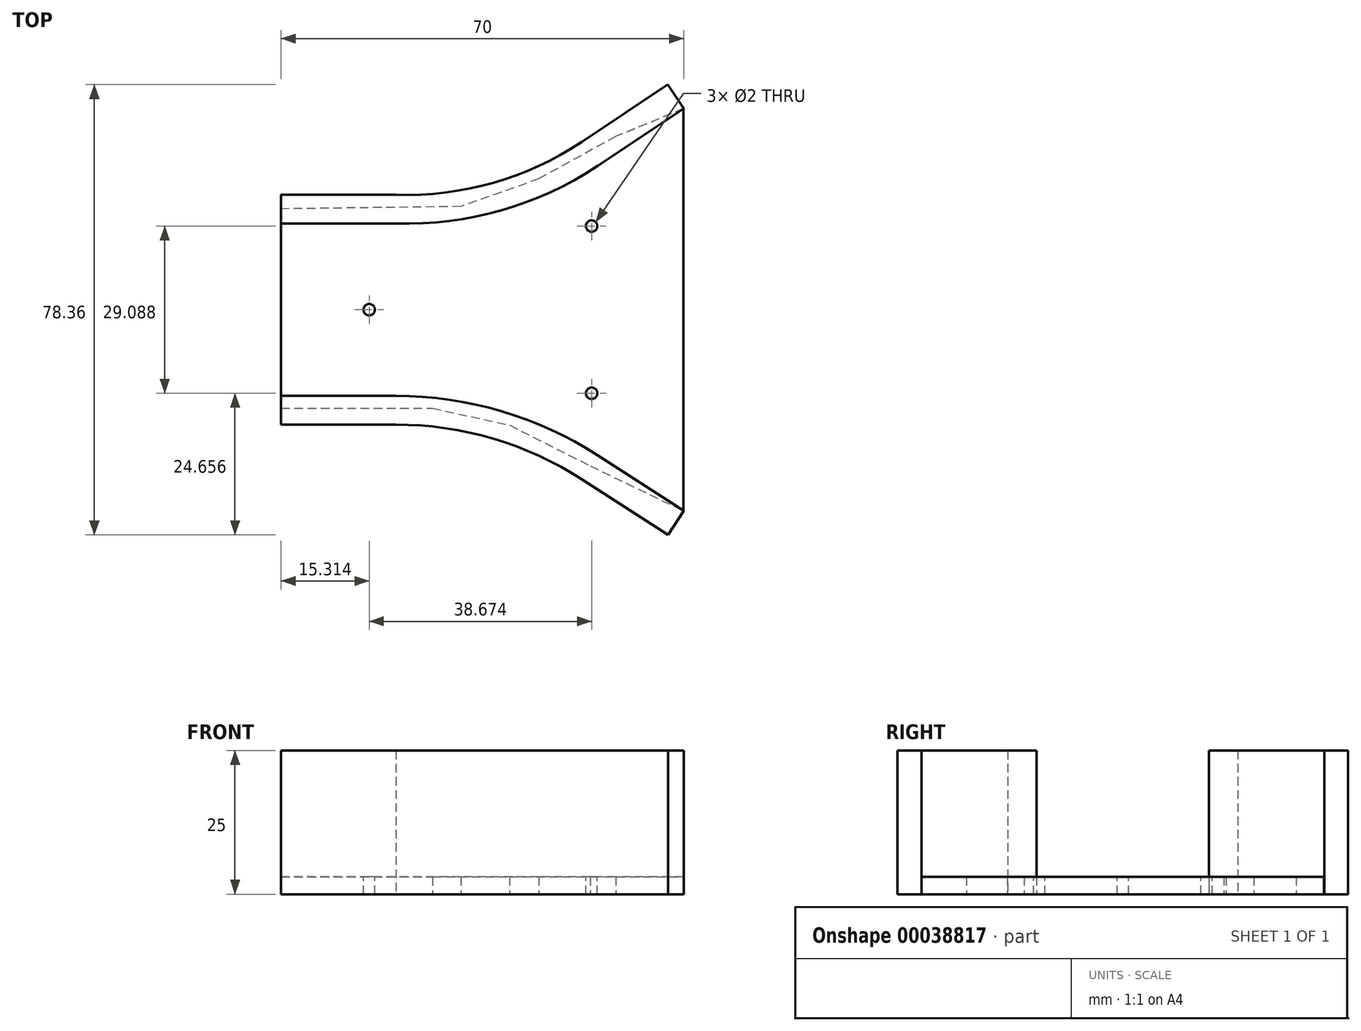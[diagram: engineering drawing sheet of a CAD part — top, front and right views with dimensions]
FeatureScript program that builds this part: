
annotation { "Feature Type Name" : "Feature", "Feature Type Description" : "" }
export const myFeature = defineFeature(function(context is Context, id is Id, definition is map)
    precondition{}
    {
        {
            var Q0;
            Q0=qCreatedBy(makeId("Top.planeOp"),FACE);
            var sketch = newSketch(context, id + "F0", { "sketchPlane" : qUnion([Q0])});
            skLineSegment(sketch, "E0", {"start": v(0, 15) * mm, "end": v(40, 15) * mm, "construction": true});
            skLineSegment(sketch, "E1", {"start": v(40, 15) * mm, "end": v(70, 35) * mm, "construction": true});
            skLineSegment(sketch, "E2", {"start": v(70, 35) * mm, "end": v(70, -35) * mm, "construction": true});
            skLineSegment(sketch, "E3", {"start": v(70, -35) * mm, "end": v(39.02, -15) * mm, "construction": true});
            skLineSegment(sketch, "E4", {"start": v(39.02, -15) * mm, "end": v(0, -15) * mm, "construction": true});
            skLineSegment(sketch, "E5", {"start": v(0, -15) * mm, "end": v(0, 15) * mm});
            skLineSegment(sketch, "E6", {"start": v(40, 38.6) * mm, "end": v(40, -30.77) * mm, "construction": true});
            skLineSegment(sketch, "E7", {"start": v(70, 35) * mm, "end": v(55, 25) * mm});
            skLineSegment(sketch, "E8", {"start": v(70, -35) * mm, "end": v(55, -25.32) * mm});
            skArc(sketch, "E9", {"start": v(55, 25) * mm, "mid": v(38.28, 17.27) * mm, "end": v(20, 15) * mm});
            skLineSegment(sketch, "E10", {"start": v(20, 39.94) * mm, "end": v(20, -33.31) * mm, "construction": true});
            skLineSegment(sketch, "E11", {"start": v(55, 46.25) * mm, "end": v(55, -47.23) * mm, "construction": true});
            skLineSegment(sketch, "E12", {"start": v(0, 15) * mm, "end": v(20, 15) * mm});
            skLineSegment(sketch, "E13", {"start": v(0, -15) * mm, "end": v(20, -15) * mm});
            skLineSegment(sketch, "E14", {"start": v(0, 20) * mm, "end": v(20, 20) * mm});
            skLineSegment(sketch, "E15", {"start": v(0, -20) * mm, "end": v(20, -20) * mm});
            skLineSegment(sketch, "E16", {"start": v(70, 35) * mm, "end": v(64.45, 43.32) * mm, "construction": true});
            skLineSegment(sketch, "E17", {"start": v(70, -35) * mm, "end": v(60.38, -49.9) * mm, "construction": true});
            skLineSegment(sketch, "E18", {"start": v(55, 25) * mm, "end": v(50.98, 31.03) * mm, "construction": true});
            skLineSegment(sketch, "E19", {"start": v(55, -25.32) * mm, "end": v(51.47, -30.78) * mm, "construction": true});
            skLineSegment(sketch, "E20", {"start": v(67.23, 39.16) * mm, "end": v(52.23, 29.16) * mm});
            skLineSegment(sketch, "E21", {"start": v(67.29, -39.2) * mm, "end": v(52.29, -29.52) * mm});
            skLineSegment(sketch, "E22", {"start": v(70, 35) * mm, "end": v(67.23, 39.16) * mm});
            skLineSegment(sketch, "E23", {"start": v(70, -35) * mm, "end": v(67.29, -39.2) * mm});
            skLineSegment(sketch, "E24", {"start": v(0, 20) * mm, "end": v(0, 15) * mm});
            skLineSegment(sketch, "E25", {"start": v(0, -15) * mm, "end": v(0, -20) * mm});
            skArc(sketch, "E26", {"start": v(52.23, 29.16) * mm, "mid": v(36.83, 22.05) * mm, "end": v(20, 20) * mm});
            skArc(sketch, "E27", {"start": v(55, -25.32) * mm, "mid": v(38.24, -17.63) * mm, "end": v(20, -15) * mm});
            skArc(sketch, "E28", {"start": v(52.29, -29.52) * mm, "mid": v(36.83, -22.43) * mm, "end": v(20, -20) * mm});
            skLineSegment(sketch, "E29", {"start": v(70, 35) * mm, "end": v(0, 35) * mm, "construction": true});
            skLineSegment(sketch, "E30", {"start": v(70, -35) * mm, "end": v(0, -35) * mm, "construction": true});
            skSolve(sketch);
        }
        {
            var Q0;
            Q0 = qSketchRegion(id + "F0", true);
            extrude(context, id + "F1", {"entities" : qUnion([Q0]), "depth" : 25 * mm});
        }
        {
            var Q0;
            Q0=qCreatedBy(makeId("Top.planeOp"),FACE);
            var sketch = newSketch(context, id + "F2", { "sketchPlane" : qUnion([Q0])});
            skLineSegment(sketch, "E31", {"start": v(0, 17.54) * mm, "end": v(0, -17.14) * mm});
            skLineSegment(sketch, "E32", {"start": v(0, -17.14) * mm, "end": v(26.32, -17.14) * mm});
            skLineSegment(sketch, "E33", {"start": v(26.32, -17.14) * mm, "end": v(39.7, -20.09) * mm});
            skLineSegment(sketch, "E34", {"start": v(39.7, -20.09) * mm, "end": v(53.77, -27.19) * mm});
            skLineSegment(sketch, "E35", {"start": v(53.77, -27.19) * mm, "end": v(69.98, -35) * mm});
            skLineSegment(sketch, "E36", {"start": v(69.98, -35) * mm, "end": v(69.98, 34.97) * mm});
            skLineSegment(sketch, "E37", {"start": v(69.98, 34.97) * mm, "end": v(58.2, 30.13) * mm});
            skLineSegment(sketch, "E38", {"start": v(58.2, 30.13) * mm, "end": v(44.8, 22.77) * mm});
            skLineSegment(sketch, "E39", {"start": v(44.8, 22.77) * mm, "end": v(31.27, 17.95) * mm});
            skLineSegment(sketch, "E40", {"start": v(31.27, 17.95) * mm, "end": v(0, 17.54) * mm});
            skSolve(sketch);
        }
        {
            var Q0;
            Q0 = qSketchRegion(id + "F2", true);
            extrude(context, id + "F3", {"entities" : qUnion([Q0]), "depth" : 3 * mm});
        }
        {
            var Q0;
            Q0=makeQuery(id+"F3.opExtrude","CAP_FACE",FACE,{"disambiguationData":[OSD([sQuery(id+"F2.wireOp",EDGE,"E31"),sQuery(id+"F2.wireOp",EDGE,"E32"),sQuery(id+"F2.wireOp",EDGE,"E33"),sQuery(id+"F2.wireOp",EDGE,"E34"),sQuery(id+"F2.wireOp",EDGE,"E35"),sQuery(id+"F2.wireOp",EDGE,"E36"),sQuery(id+"F2.wireOp",EDGE,"E37"),sQuery(id+"F2.wireOp",EDGE,"E38"),sQuery(id+"F2.wireOp",EDGE,"E39"),sQuery(id+"F2.wireOp",EDGE,"E40")])],"isStart":false});
            var sketch = newSketch(context, id + "F4", { "sketchPlane" : qUnion([Q0])});
            skCircle(sketch, "E41", {"center": v(15.31, 0) * mm, "radius": 1 * mm});
            skLineSegment(sketch, "E42", {"start": v(53.99, 17.16) * mm, "end": v(53.99, -21.37) * mm, "construction": true});
            skCircle(sketch, "E43", {"center": v(53.99, 14.54) * mm, "radius": 1 * mm});
            skCircle(sketch, "E44", {"center": v(53.99, -14.54) * mm, "radius": 1 * mm});
            skSolve(sketch);
        }
        {
            var Q0;
            Q0 = qSketchRegion(id + "F4", true);
            extrude(context, id + "F5", {"entities" : qUnion([Q0]), "operationType" : NewBodyOperationType.REMOVE, "oppositeDirection" : true, "depth" : 3 * mm});
        }
    });
